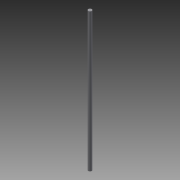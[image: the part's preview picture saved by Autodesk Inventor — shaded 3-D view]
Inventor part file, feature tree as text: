
AUTODESK INVENTOR PART (.ipt)
format: ipt  version: 2013 (Build 170138000, 138)  size: 60,928 bytes
history: native  units: in
note: dims shown in document units (in); Inventor stores cm internally (conversion verified against a paired STEP export)
features: extrude x1, sketch x1
ambient origin geometry x8: Origin, YZ Plane, XZ Plane, XY Plane, X Axis, Y Axis, Z Axis, Center Point
bodies: Solid1 (feature_tree)
feature tree (2):
  extrude  "Extrusion1"  Depth=20.0in TaperAngle=0.0deg
  sketch  "Sketch1"  dims[d0=0.5in d1=20.0in d2=0.0in]
